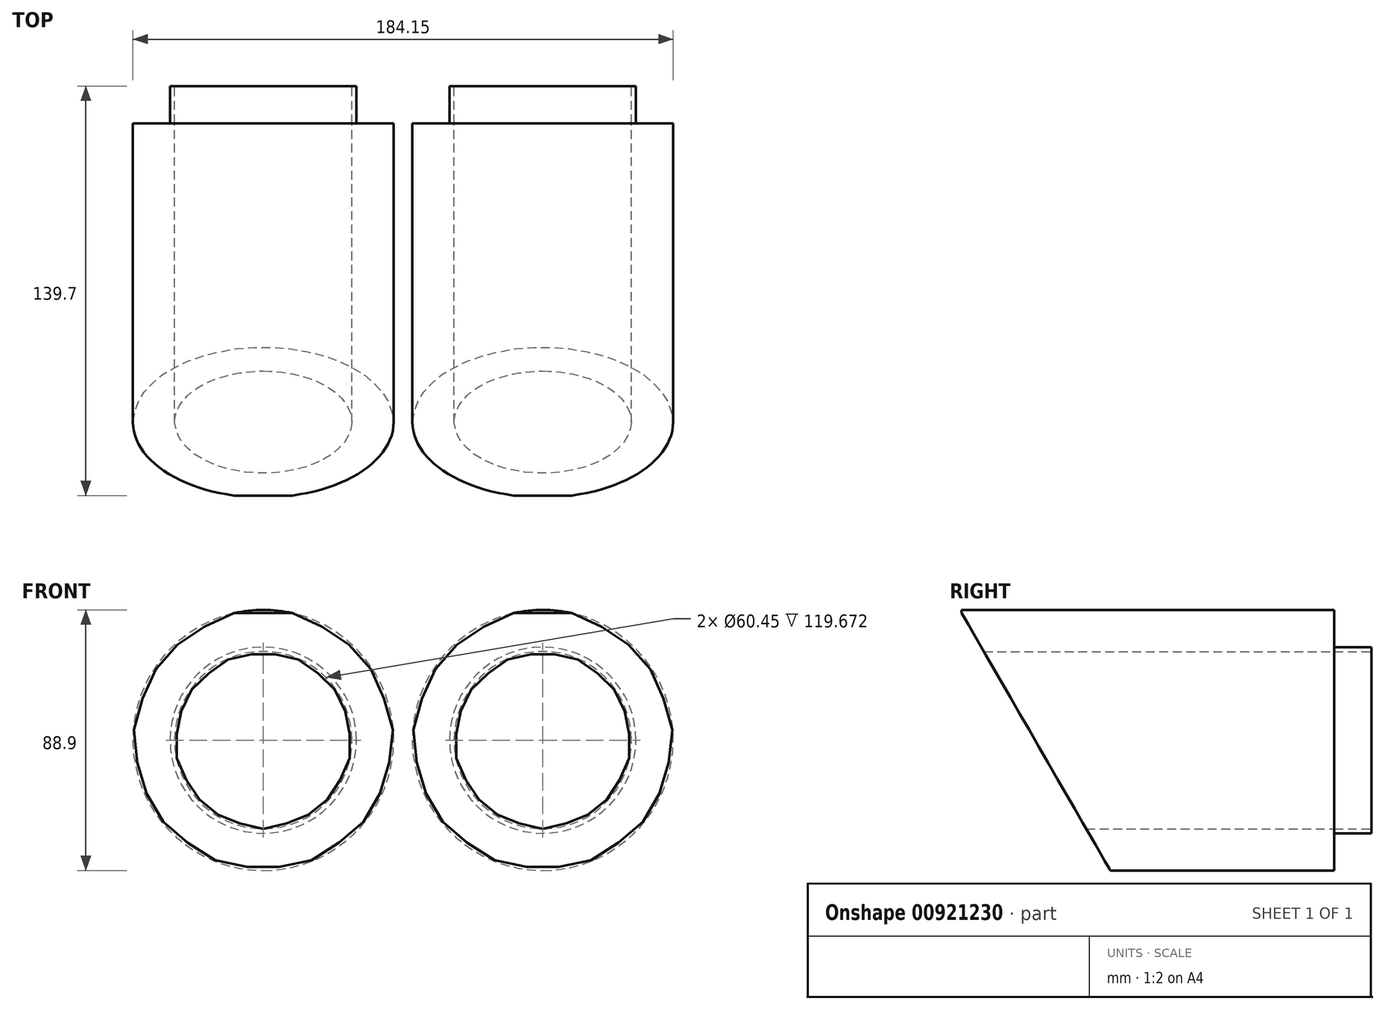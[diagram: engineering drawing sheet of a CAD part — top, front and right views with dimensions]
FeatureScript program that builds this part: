
annotation { "Feature Type Name" : "Feature", "Feature Type Description" : "" }
export const myFeature = defineFeature(function(context is Context, id is Id, definition is map)
    precondition{}
    {
        {
            var Q0;
            Q0=qCreatedBy(makeId("Front.planeOp"),FACE);
            var sketch = newSketch(context, id + "F0", { "sketchPlane" : qUnion([Q0])});
            skCircle(sketch, "E0", {"center": v(-38.32, 0) * mm, "radius": 44.45 * mm});
            skCircle(sketch, "E1", {"center": v(56.93, 0) * mm, "radius": 44.45 * mm});
            skLineSegment(sketch, "E2", {"start": v(6.13, 0) * mm, "end": v(12.48, 0) * mm});
            skSolve(sketch);
        }
        {
            var Q0;
            Q0=makeQuery(id+"F0.imprint","IMPRINT",FACE,{"disambiguationData":[TD([[makeQuery(id+"F0.imprint","IMPRINT",EDGE,{"derivedFrom":sQuery(id+"F0.wireOp",EDGE,"E0")}),1.0]])]});
            var Q1;
            Q1=makeQuery(id+"F0.imprint","IMPRINT",FACE,{"disambiguationData":[TD([[makeQuery(id+"F0.imprint","IMPRINT",EDGE,{"derivedFrom":sQuery(id+"F0.wireOp",EDGE,"E1")}),1.0]])]});
            extrude(context, id + "F1", {"entities" : qUnion([Q0, Q1]), "depth" : 127 * mm, "offsetDistance" : 25.4 * mm});
        }
        {
            var Q0;
            Q0=makeQuery(id+"F1.opExtrude","CAP_FACE",FACE,{"disambiguationData":[OSD([sQuery(id+"F0.wireOp",EDGE,"E0")])],"isStart":true});
            var sketch = newSketch(context, id + "F2", { "sketchPlane" : qUnion([Q0])});
            skCircle(sketch, "E3", {"center": v(38.32, 0) * mm, "radius": 31.75 * mm});
            skCircle(sketch, "E4", {"center": v(-56.93, 0) * mm, "radius": 31.75 * mm});
            skSolve(sketch);
        }
        {
            var Q0;
            Q0=makeQuery(id+"F2.imprint","IMPRINT",FACE,{"disambiguationData":[TD([[makeQuery(id+"F2.imprint","IMPRINT",EDGE,{"derivedFrom":sQuery(id+"F2.wireOp",EDGE,"E3")}),1.0]])]});
            var Q1;
            Q1=makeQuery(id+"F2.imprint","IMPRINT",FACE,{"disambiguationData":[TD([[makeQuery(id+"F2.imprint","IMPRINT",EDGE,{"derivedFrom":sQuery(id+"F2.wireOp",EDGE,"E4")}),1.0]])]});
            extrude(context, id + "F3", {"entities" : qUnion([Q0, Q1]), "depth" : 12.7 * mm, "offsetDistance" : 25.4 * mm});
        }
        {
            var Q0;
            Q0=makeQuery(id+"F3.opExtrude","CAP_FACE",FACE,{"disambiguationData":[OSD([sQuery(id+"F2.wireOp",EDGE,"E3")])],"isStart":false});
            var sketch = newSketch(context, id + "F4", { "sketchPlane" : qUnion([Q0])});
            skCircle(sketch, "E5.0", {"center": v(38.32, 0) * mm, "radius": 31.75 * mm});
            skCircle(sketch, "E6.0", {"center": v(-56.93, 0) * mm, "radius": 31.75 * mm});
            skCircle(sketch, "E7.0", {"center": v(38.32, 0) * mm, "radius": 30.23 * mm});
            skCircle(sketch, "E8.0", {"center": v(-56.93, 0) * mm, "radius": 30.23 * mm});
            skSolve(sketch);
        }
        {
            var Q0;
            Q0=makeQuery(id+"F4.imprint","IMPRINT",FACE,{"disambiguationData":[TD([[makeQuery(id+"F4.imprint","IMPRINT",EDGE,{"derivedFrom":sQuery(id+"F4.wireOp",EDGE,"E8.0")}),1.0]])]});
            var Q1;
            Q1=makeQuery(id+"F4.imprint","IMPRINT",FACE,{"disambiguationData":[TD([[makeQuery(id+"F4.imprint","IMPRINT",EDGE,{"derivedFrom":sQuery(id+"F4.wireOp",EDGE,"E7.0")}),1.0]])]});
            extrude(context, id + "F5", {"entities" : qUnion([Q0, Q1]), "operationType" : NewBodyOperationType.REMOVE, "endBound" : BoundingType.THROUGH_ALL, "oppositeDirection" : true, "depth" : 25.4 * mm, "offsetDistance" : 25.4 * mm});
        }
        {
            var Q0;
            Q0=qCreatedBy(makeId("Right.planeOp"),FACE);
            var sketch = newSketch(context, id + "F6", { "sketchPlane" : qUnion([Q0])});
            skLineSegment(sketch, "E9", {"start": v(-133.02, 53.76) * mm, "end": v(-59.11, -74.25) * mm});
            skLineSegment(sketch, "E10", {"start": v(-59.11, -74.25) * mm, "end": v(-133.02, -74.25) * mm});
            skLineSegment(sketch, "E11", {"start": v(-133.02, -74.25) * mm, "end": v(-133.02, 53.76) * mm});
            skSolve(sketch);
        }
        {
            var Q0;
            Q0=makeQuery(id+"F6.imprint","IMPRINT",FACE,{"disambiguationData":[TD([[makeQuery(id+"F6.imprint","IMPRINT",EDGE,{"derivedFrom":sQuery(id+"F6.wireOp",EDGE,"E9")}),-1.0]])]});
            extrude(context, id + "F7", {"entities" : qUnion([Q0]), "operationType" : NewBodyOperationType.REMOVE, "endBound" : BoundingType.THROUGH_ALL, "oppositeDirection" : true, "depth" : 25.4 * mm, "offsetDistance" : 25.4 * mm, "hasSecondDirection" : true, "secondDirectionBound" : SecondDirectionBoundingType.THROUGH_ALL, "secondDirectionOppositeDirection" : false, "secondDirectionDepth" : 25.4 * mm});
        }
    });
